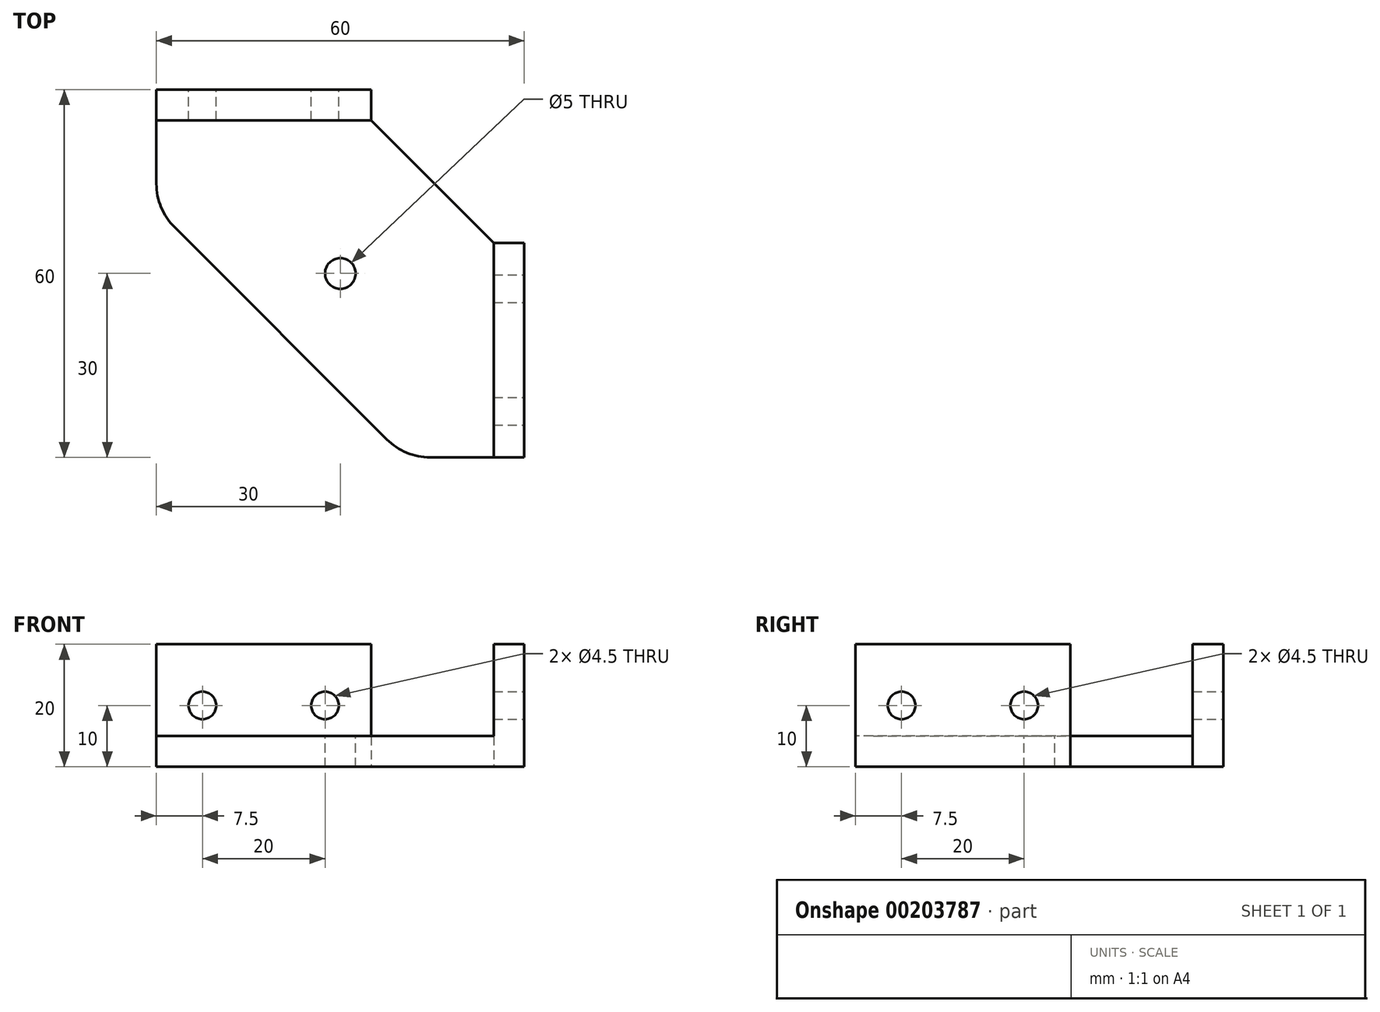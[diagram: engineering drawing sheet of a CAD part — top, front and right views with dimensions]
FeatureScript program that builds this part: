
annotation { "Feature Type Name" : "Feature", "Feature Type Description" : "" }
export const myFeature = defineFeature(function(context is Context, id is Id, definition is map)
    precondition{}
    {
        {
            var Q0;
            Q0=qCreatedBy(makeId("Top.planeOp"),FACE);
            var sketch = newSketch(context, id + "F0", { "sketchPlane" : qUnion([Q0])});
            skLineSegment(sketch, "E0.bottom", {"start": v(30, -30) * mm, "end": v(10.5, -30) * mm});
            skLineSegment(sketch, "E0.top", {"start": v(5, 30) * mm, "end": v(-30, 30) * mm});
            skLineSegment(sketch, "E0.left", {"start": v(30, -30) * mm, "end": v(30, 5) * mm});
            skLineSegment(sketch, "E0.right", {"start": v(-30, 10.5) * mm, "end": v(-30, 30) * mm});
            skPoint(sketch, "E0.middle", {"position": v(0, 0) * mm});
            skLineSegment(sketch, "E1.0", {"start": v(25, -30) * mm, "end": v(25, 5) * mm});
            skLineSegment(sketch, "E2.0", {"start": v(30, 5) * mm, "end": v(25, 5) * mm});
            skLineSegment(sketch, "E3.trimOffspring", {"start": v(5, 25) * mm, "end": v(-30, 25) * mm});
            skLineSegment(sketch, "E4.trimOffspring", {"start": v(5, 25) * mm, "end": v(5, 30) * mm});
            skLineSegment(sketch, "E5", {"start": v(25, 5) * mm, "end": v(5, 25) * mm});
            skLineSegment(sketch, "E6.0", {"start": v(0.25, -19.75) * mm, "end": v(-19.75, 0.25) * mm});
            skLineSegment(sketch, "E7", {"start": v(-19.75, 0.25) * mm, "end": v(-30, 10.5) * mm});
            skLineSegment(sketch, "E8", {"start": v(0.25, -19.75) * mm, "end": v(10.5, -30) * mm});
            skPoint(sketch, "E9.orphan", {"position": v(-30, -30) * mm});
            skPoint(sketch, "E10.orphan", {"position": v(30, 30) * mm});
            skSolve(sketch);
        }
        {
            var Q0;
            {var subQ3=sQuery(id+"F0.wireOp",EDGE,"E1.0");Q0=makeQuery(id+"F0.imprint","IMPRINT",FACE,{"disambiguationData":[TD([[makeQuery(id+"F0.imprint","IMPRINT",EDGE,{"derivedFrom":subQ3}),1.0]])]});}
            var Q1;
            {var subQ0=sQuery(id+"F0.wireOp",EDGE,"E0.top");Q1=makeQuery(id+"F0.imprint","IMPRINT",FACE,{"disambiguationData":[TD([[makeQuery(id+"F0.imprint","IMPRINT",EDGE,{"derivedFrom":subQ0}),1.0]])]});}
            var Q2;
            {var subQ0=sQuery(id+"F0.wireOp",EDGE,"E0.left");Q2=makeQuery(id+"F0.imprint","IMPRINT",FACE,{"disambiguationData":[TD([[makeQuery(id+"F0.imprint","IMPRINT",EDGE,{"derivedFrom":subQ0}),1.0]])]});}
            extrude(context, id + "F1", {"entities" : qUnion([Q0, Q1, Q2]), "depth" : 5 * mm});
        }
        {
            var Q0;
            Q0=makeQuery(id+"F1.opExtrude","CAP_FACE",FACE,{"disambiguationData":[OSD([sQuery(id+"F0.wireOp",EDGE,"E0.bottom"),sQuery(id+"F0.wireOp",EDGE,"E0.top"),sQuery(id+"F0.wireOp",EDGE,"E0.left"),sQuery(id+"F0.wireOp",EDGE,"E0.right"),sQuery(id+"F0.wireOp",EDGE,"E2.0"),sQuery(id+"F0.wireOp",EDGE,"E4.trimOffspring"),sQuery(id+"F0.wireOp",EDGE,"E5"),sQuery(id+"F0.wireOp",EDGE,"E6.0"),sQuery(id+"F0.wireOp",EDGE,"E7"),sQuery(id+"F0.wireOp",EDGE,"E8")])],"isStart":false});
            var sketch = newSketch(context, id + "F2", { "sketchPlane" : qUnion([Q0])});
            skLineSegment(sketch, "E11", {"start": v(5, 25) * mm, "end": v(-30, 25) * mm});
            skLineSegment(sketch, "E12", {"start": v(-30, 25) * mm, "end": v(-30, 30) * mm});
            skLineSegment(sketch, "E13", {"start": v(-30, 30) * mm, "end": v(5, 30) * mm});
            skLineSegment(sketch, "E14", {"start": v(5, 30) * mm, "end": v(5, 25) * mm});
            skLineSegment(sketch, "E15", {"start": v(25, 5) * mm, "end": v(25, -30) * mm});
            skLineSegment(sketch, "E16", {"start": v(25, -30) * mm, "end": v(30, -30) * mm});
            skLineSegment(sketch, "E17", {"start": v(30, -30) * mm, "end": v(30, 5) * mm});
            skLineSegment(sketch, "E18", {"start": v(30, 5) * mm, "end": v(25, 5) * mm});
            skSolve(sketch);
        }
        {
            var Q0;
            Q0=makeQuery(id+"F2.imprint","IMPRINT",FACE,{"disambiguationData":[TD([[makeQuery(id+"F2.imprint","IMPRINT",EDGE,{"derivedFrom":sQuery(id+"F2.wireOp",EDGE,"E11")}),-1.0]])]});
            var Q1;
            Q1=makeQuery(id+"F2.imprint","IMPRINT",FACE,{"disambiguationData":[TD([[makeQuery(id+"F2.imprint","IMPRINT",EDGE,{"derivedFrom":sQuery(id+"F2.wireOp",EDGE,"E15")}),1.0]])]});
            extrude(context, id + "F3", {"entities" : qUnion([Q0, Q1]), "operationType" : NewBodyOperationType.ADD, "depth" : 15 * mm});
        }
        {
            var Q0;
            Q0=makeQuery(id+"F1.opExtrude","CAP_FACE",FACE,{"disambiguationData":[OSD([sQuery(id+"F0.wireOp",EDGE,"E0.bottom"),sQuery(id+"F0.wireOp",EDGE,"E0.top"),sQuery(id+"F0.wireOp",EDGE,"E0.left"),sQuery(id+"F0.wireOp",EDGE,"E0.right"),sQuery(id+"F0.wireOp",EDGE,"E2.0"),sQuery(id+"F0.wireOp",EDGE,"E4.trimOffspring"),sQuery(id+"F0.wireOp",EDGE,"E5"),sQuery(id+"F0.wireOp",EDGE,"E6.0"),sQuery(id+"F0.wireOp",EDGE,"E7"),sQuery(id+"F0.wireOp",EDGE,"E8")])],"isStart":false});
            var sketch = newSketch(context, id + "F4", { "sketchPlane" : qUnion([Q0])});
            skCircle(sketch, "E19", {"center": v(0, 0) * mm, "radius": 2.5 * mm});
            skSolve(sketch);
        }
        {
            var Q0;
            Q0=makeQuery(id+"F4.imprint","IMPRINT",FACE,{"disambiguationData":[TD([[makeQuery(id+"F4.imprint","IMPRINT",EDGE,{"derivedFrom":sQuery(id+"F4.wireOp",EDGE,"E19")}),1.0]])]});
            extrude(context, id + "F5", {"entities" : qUnion([Q0]), "operationType" : NewBodyOperationType.REMOVE, "endBound" : BoundingType.UP_TO_NEXT, "oppositeDirection" : true, "depth" : 25 * mm});
        }
        {
            var Q0;
            Q0=makeQuery(id+"F3.boolean.opBoolean","MERGE",FACE,{"derivedFrom":[makeQuery(id+"F1.opExtrude","SWEPT_FACE",FACE,{"disambiguationData":[OSD([sQuery(id+"F0.wireOp",EDGE,"E0.left")])]}),makeQuery(id+"F3.opExtrude","SWEPT_FACE",FACE,{"disambiguationData":[OSD([sQuery(id+"F2.wireOp",EDGE,"E17")])]})]});
            var sketch = newSketch(context, id + "F6", { "sketchPlane" : qUnion([Q0])});
            skLineSegment(sketch, "E20", {"start": v(-30, 0) * mm, "end": v(-22.5, 0) * mm, "construction": true});
            skLineSegment(sketch, "E21", {"start": v(-22.5, 0) * mm, "end": v(-22.5, 10) * mm, "construction": true});
            skLineSegment(sketch, "E22", {"start": v(-22.5, 10) * mm, "end": v(-2.5, 10) * mm, "construction": true});
            skCircle(sketch, "E23", {"center": v(-22.5, 10) * mm, "radius": 2.25 * mm});
            skCircle(sketch, "E24", {"center": v(-2.5, 10) * mm, "radius": 2.25 * mm});
            skSolve(sketch);
        }
        {
            var Q0;
            Q0=makeQuery(id+"F6.imprint","IMPRINT",FACE,{"disambiguationData":[TD([[makeQuery(id+"F6.imprint","IMPRINT",EDGE,{"derivedFrom":sQuery(id+"F6.wireOp",EDGE,"E23")}),1.0]])]});
            var Q1;
            Q1=makeQuery(id+"F6.imprint","IMPRINT",FACE,{"disambiguationData":[TD([[makeQuery(id+"F6.imprint","IMPRINT",EDGE,{"derivedFrom":sQuery(id+"F6.wireOp",EDGE,"E24")}),1.0]])]});
            extrude(context, id + "F7", {"entities" : qUnion([Q0, Q1]), "operationType" : NewBodyOperationType.REMOVE, "endBound" : BoundingType.UP_TO_NEXT, "oppositeDirection" : true, "depth" : 25 * mm});
        }
        {
            var Q0;
            Q0=makeQuery(id+"F3.boolean.opBoolean","MERGE",FACE,{"derivedFrom":[makeQuery(id+"F1.opExtrude","SWEPT_FACE",FACE,{"disambiguationData":[OSD([sQuery(id+"F0.wireOp",EDGE,"E0.top")])]}),makeQuery(id+"F3.opExtrude","SWEPT_FACE",FACE,{"disambiguationData":[OSD([sQuery(id+"F2.wireOp",EDGE,"E13")])]})]});
            var sketch = newSketch(context, id + "F8", { "sketchPlane" : qUnion([Q0])});
            skLineSegment(sketch, "E25", {"start": v(30, 0) * mm, "end": v(22.5, 0) * mm, "construction": true});
            skLineSegment(sketch, "E26", {"start": v(22.5, 0) * mm, "end": v(22.5, 10) * mm, "construction": true});
            skLineSegment(sketch, "E27", {"start": v(22.5, 10) * mm, "end": v(2.5, 10) * mm, "construction": true});
            skCircle(sketch, "E28", {"center": v(2.5, 10) * mm, "radius": 2.25 * mm});
            skCircle(sketch, "E29", {"center": v(22.5, 10) * mm, "radius": 2.25 * mm});
            skSolve(sketch);
        }
        {
            var Q0;
            Q0=makeQuery(id+"F8.imprint","IMPRINT",FACE,{"disambiguationData":[TD([[makeQuery(id+"F8.imprint","IMPRINT",EDGE,{"derivedFrom":sQuery(id+"F8.wireOp",EDGE,"E28")}),1.0]])]});
            var Q1;
            Q1=makeQuery(id+"F8.imprint","IMPRINT",FACE,{"disambiguationData":[TD([[makeQuery(id+"F8.imprint","IMPRINT",EDGE,{"derivedFrom":sQuery(id+"F8.wireOp",EDGE,"E29")}),1.0]])]});
            extrude(context, id + "F9", {"entities" : qUnion([Q0, Q1]), "operationType" : NewBodyOperationType.REMOVE, "endBound" : BoundingType.UP_TO_NEXT, "oppositeDirection" : true, "depth" : 25 * mm});
        }
        {
            var Q0;
            Q0=makeQuery(id+"F1.opExtrude","SWEPT_EDGE",EDGE,{"disambiguationData":[OSD([sQuery(id+"F0.wireOp",EDGE,"E0.right"),sQuery(id+"F0.wireOp",EDGE,"E7")])]});
            var Q1;
            Q1=makeQuery(id+"F1.opExtrude","SWEPT_EDGE",EDGE,{"disambiguationData":[OSD([sQuery(id+"F0.wireOp",EDGE,"E0.bottom"),sQuery(id+"F0.wireOp",EDGE,"E8")])]});
            fillet(context, id + "F10", {"entities" : qUnion([Q0, Q1]), "radius" : 10 * mm, "tangentPropagation" : true, "allowEdgeOverflow" : false});
        }
    });
